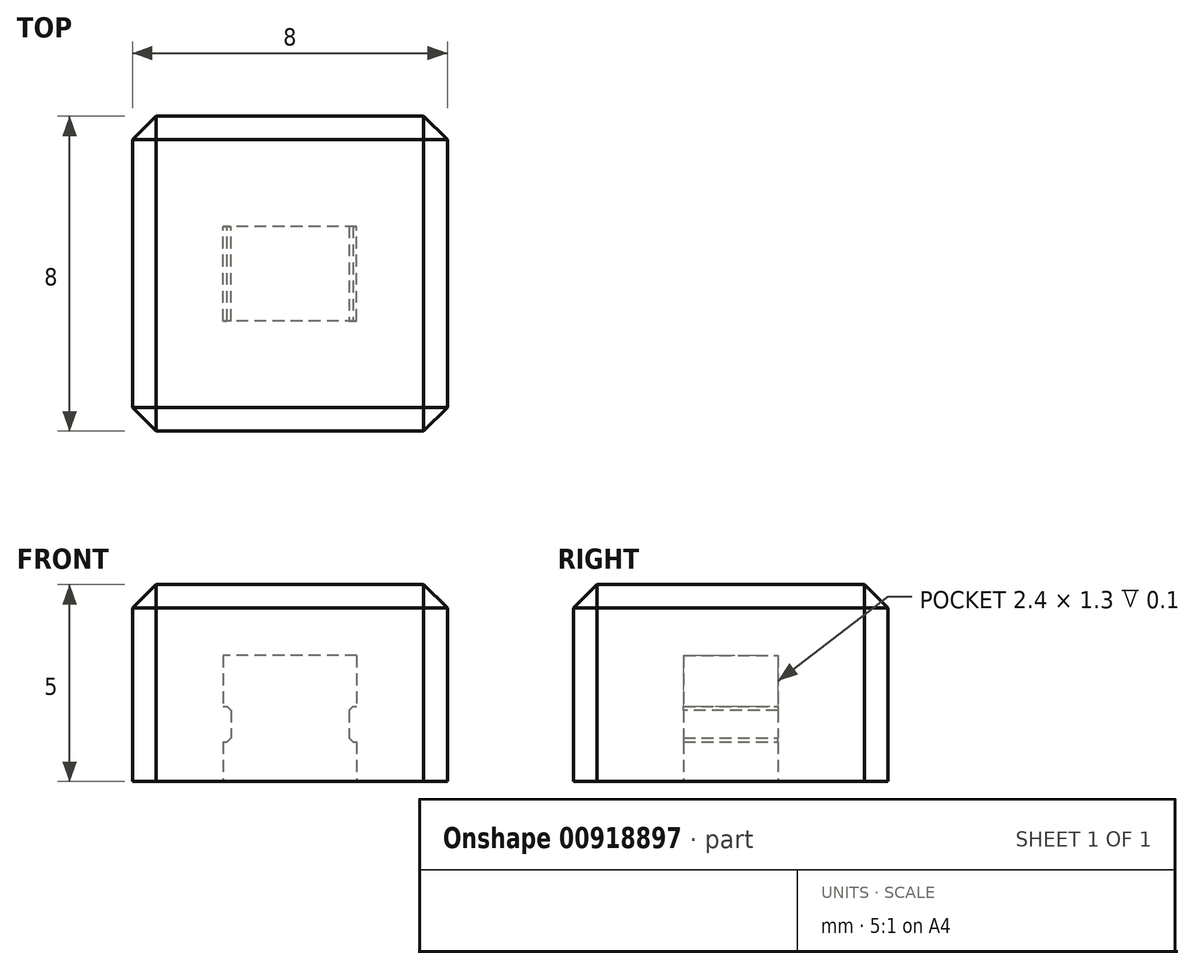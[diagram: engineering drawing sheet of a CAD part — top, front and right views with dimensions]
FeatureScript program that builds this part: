
annotation { "Feature Type Name" : "Feature", "Feature Type Description" : "" }
export const myFeature = defineFeature(function(context is Context, id is Id, definition is map)
    precondition{}
    {
        {
            var Q0;
            Q0=qCreatedBy(makeId("Top.planeOp"),FACE);
            var sketch = newSketch(context, id + "F0", { "sketchPlane" : qUnion([Q0])});
            skLineSegment(sketch, "E0.bottom", {"start": v(4, -4) * mm, "end": v(-4, -4) * mm});
            skLineSegment(sketch, "E0.top", {"start": v(4, 4) * mm, "end": v(-4, 4) * mm});
            skLineSegment(sketch, "E0.left", {"start": v(4, -4) * mm, "end": v(4, 4) * mm});
            skLineSegment(sketch, "E0.right", {"start": v(-4, -4) * mm, "end": v(-4, 4) * mm});
            skPoint(sketch, "E0.middle", {"position": v(0, 0) * mm});
            skSolve(sketch);
        }
        {
            var Q0;
            Q0 = qSketchRegion(id + "F0", true);
            extrude(context, id + "F1", {"entities" : qUnion([Q0]), "depth" : 5 * mm, "offsetDistance" : 25 * mm});
        }
        {
            var Q0;
            Q0=qCreatedBy(makeId("Top.planeOp"),FACE);
            var sketch = newSketch(context, id + "F2", { "sketchPlane" : qUnion([Q0])});
            skLineSegment(sketch, "E1.bottom", {"start": v(1.7, -1.2) * mm, "end": v(-1.7, -1.2) * mm});
            skLineSegment(sketch, "E1.top", {"start": v(1.7, 1.2) * mm, "end": v(-1.7, 1.2) * mm});
            skLineSegment(sketch, "E1.left", {"start": v(1.7, -1.2) * mm, "end": v(1.7, 1.2) * mm});
            skLineSegment(sketch, "E1.right", {"start": v(-1.7, -1.2) * mm, "end": v(-1.7, 1.2) * mm});
            skPoint(sketch, "E1.middle", {"position": v(0, 0) * mm});
            skSolve(sketch);
        }
        {
            var Q0;
            Q0 = qSketchRegion(id + "F2", true);
            extrude(context, id + "F3", {"entities" : qUnion([Q0]), "operationType" : NewBodyOperationType.REMOVE, "depth" : 3.2 * mm, "offsetDistance" : 25 * mm});
        }
        {
            var Q0;
            Q0=qCreatedBy(makeId("Top.planeOp"),FACE);
            cPlane(context, id + "F4", {"entities" : qUnion([Q0]), "cplaneType" : CPlaneType.OFFSET, "offset" : 1 * mm, "width" : 150 * mm, "height" : 150 * mm});
        }
        {
            var Q0;
            Q0=qCreatedBy(id+"F4.planeOp",FACE);
            var sketch = newSketch(context, id + "F5", { "sketchPlane" : qUnion([Q0])});
            skPoint(sketch, "E2.middle", {"position": v(0, 0) * mm});
            skLineSegment(sketch, "E3.bottom", {"start": v(-1.7, -1.2) * mm, "end": v(-1.5, -1.2) * mm});
            skLineSegment(sketch, "E3.top", {"start": v(-1.7, 1.2) * mm, "end": v(-1.5, 1.2) * mm});
            skLineSegment(sketch, "E3.left", {"start": v(-1.7, -1.2) * mm, "end": v(-1.7, 1.2) * mm});
            skLineSegment(sketch, "E3.right", {"start": v(-1.5, -1.2) * mm, "end": v(-1.5, 1.2) * mm});
            skLineSegment(sketch, "E4.bottom", {"start": v(1.5, -1.2) * mm, "end": v(1.7, -1.2) * mm});
            skLineSegment(sketch, "E4.top", {"start": v(1.5, 1.2) * mm, "end": v(1.7, 1.2) * mm});
            skLineSegment(sketch, "E4.left", {"start": v(1.5, -1.2) * mm, "end": v(1.5, 1.2) * mm});
            skLineSegment(sketch, "E4.right", {"start": v(1.7, -1.2) * mm, "end": v(1.7, 1.2) * mm});
            skSolve(sketch);
        }
        {
            var Q0;
            Q0 = qSketchRegion(id + "F5", true);
            extrude(context, id + "F6", {"entities" : qUnion([Q0]), "operationType" : NewBodyOperationType.ADD, "depth" : 0.9 * mm, "offsetDistance" : 25 * mm});
        }
        {
            var Q0;
            Q0=makeQuery(id+"F6.opExtrude","CAP_EDGE",EDGE,{"disambiguationData":[OSD([sQuery(id+"F5.wireOp",EDGE,"E3.right")])],"isStart":true});
            var Q1;
            Q1=makeQuery(id+"F6.opExtrude","CAP_EDGE",EDGE,{"disambiguationData":[OSD([sQuery(id+"F5.wireOp",EDGE,"E3.right")])],"isStart":false});
            var Q2;
            Q2=makeQuery(id+"F6.opExtrude","CAP_EDGE",EDGE,{"disambiguationData":[OSD([sQuery(id+"F5.wireOp",EDGE,"E4.left")])],"isStart":true});
            var Q3;
            Q3=makeQuery(id+"F6.opExtrude","CAP_EDGE",EDGE,{"disambiguationData":[OSD([sQuery(id+"F5.wireOp",EDGE,"E4.left")])],"isStart":false});
            chamfer(context, id + "F7", {"entities" : qUnion([Q0, Q1, Q2, Q3]), "width" : 0.1 * mm, "tangentPropagation" : true});
        }
        {
            var Q0;
            Q0=makeQuery(id+"F1.opExtrude","CAP_EDGE",EDGE,{"disambiguationData":[OSD([sQuery(id+"F0.wireOp",EDGE,"E0.left")])],"isStart":false});
            var Q1;
            Q1=makeQuery(id+"F1.opExtrude","CAP_EDGE",EDGE,{"disambiguationData":[OSD([sQuery(id+"F0.wireOp",EDGE,"E0.right")])],"isStart":false});
            var Q2;
            Q2=makeQuery(id+"F1.opExtrude","CAP_EDGE",EDGE,{"disambiguationData":[OSD([sQuery(id+"F0.wireOp",EDGE,"E0.bottom")])],"isStart":false});
            var Q3;
            Q3=makeQuery(id+"F1.opExtrude","CAP_EDGE",EDGE,{"disambiguationData":[OSD([sQuery(id+"F0.wireOp",EDGE,"E0.top")])],"isStart":false});
            var Q4;
            Q4=makeQuery(id+"F1.opExtrude","SWEPT_EDGE",EDGE,{"disambiguationData":[OSD([sQuery(id+"F0.wireOp",EDGE,"E0.bottom"),sQuery(id+"F0.wireOp",EDGE,"E0.left")])]});
            var Q5;
            Q5=makeQuery(id+"F1.opExtrude","SWEPT_EDGE",EDGE,{"disambiguationData":[OSD([sQuery(id+"F0.wireOp",EDGE,"E0.top"),sQuery(id+"F0.wireOp",EDGE,"E0.left")])]});
            var Q6;
            Q6=makeQuery(id+"F1.opExtrude","SWEPT_EDGE",EDGE,{"disambiguationData":[OSD([sQuery(id+"F0.wireOp",EDGE,"E0.bottom"),sQuery(id+"F0.wireOp",EDGE,"E0.right")])]});
            var Q7;
            Q7=makeQuery(id+"F1.opExtrude","SWEPT_EDGE",EDGE,{"disambiguationData":[OSD([sQuery(id+"F0.wireOp",EDGE,"E0.top"),sQuery(id+"F0.wireOp",EDGE,"E0.right")])]});
            chamfer(context, id + "F8", {"entities" : qUnion([Q0, Q1, Q2, Q3, Q4, Q5, Q6, Q7]), "width" : 0.6 * mm, "tangentPropagation" : true});
        }
    });
